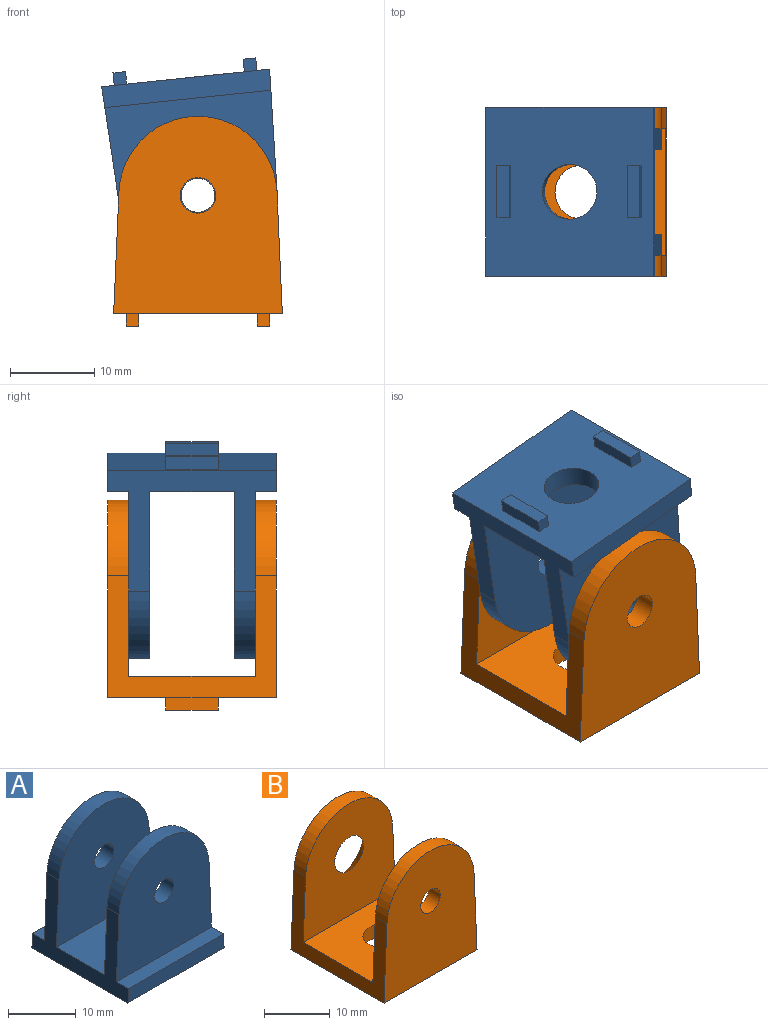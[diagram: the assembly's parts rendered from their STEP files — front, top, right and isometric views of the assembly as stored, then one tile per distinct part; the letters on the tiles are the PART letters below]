
ASSEMBLY  parts=2 mates=1
PART A: 27 faces, bbox 20x20x24.9 mm
  f0: plane 20.02x20mm, normal (0,0,-1), area 348.6mm2, adj f2,f4,f9,f10,f11,f12,f14,f15
  f1: plane 20.89x19.8mm, normal (0,1,0), area 347.9mm2, adj f2,f3,f4,f5,f8
  f2: plane 20x14.41mm, normal (1,0,0.04), area 109.7mm2, adj f0,f1,f3,f6,f7,f8,f9,f19
  f3: cylinder r=9.39mm len=18.76mm, axis (0,1,0), area 71.7mm2, adj f1,f2,f4,f6
  f4: plane 20x14.41mm, normal (-1,0,0.04), area 109.7mm2, adj f0,f1,f3,f6,f7,f8,f9,f19
  f5: cylinder r=2mm len=4mm, axis (0,1,0), area 31.4mm2, adj f1,f6
  f6: plane 20.89x19.8mm, normal (0,-1,0), area 347.9mm2, adj f2,f3,f4,f5,f7
  f7: plane 19.8x10mm, normal (0,0,1), area 164.8mm2, adj f2,f4,f6,f18,f22
  f8: plane 19.8x2.5mm, normal (0,0,1), area 49.5mm2, adj f1,f2,f4,f9
  f9: plane 20.02x2.5mm, normal (0,1,0), area 49.8mm2, adj f0,f2,f4,f8
  f10: plane 6.2x1.5mm, normal (-1,0,0), area 9.3mm2, adj f0,f11,f13,f25
  f11: plane 1.5x1.5mm, normal (0,1,0), area 2.2mm2, adj f0,f10,f12,f13
  f12: plane 6.2x1.5mm, normal (1,0,0), area 9.3mm2, adj f0,f11,f13,f25
  f13: plane 6.2x1.5mm, normal (0,0,-1), area 9.3mm2, adj f10,f11,f12,f25
  f14: plane 6.2x1.5mm, normal (-1,0,0), area 9.3mm2, adj f0,f15,f17,f26
  f15: plane 1.5x1.5mm, normal (0,1,0), area 2.2mm2, adj f0,f14,f16,f17
  f16: plane 6.2x1.5mm, normal (1,0,0), area 9.3mm2, adj f0,f15,f17,f26
  f17: plane 6.2x1.5mm, normal (0,0,-1), area 9.3mm2, adj f14,f15,f16,f26
  f18: cylinder r=3.25mm len=6.5mm, axis (0,0,-1), area 51.1mm2, adj f0,f7
  f19: plane 20.89x19.8mm, normal (0,-1,0), area 347.9mm2, adj f2,f4,f20,f21,f23
  f20: cylinder r=9.39mm len=18.76mm, axis (0,-1,0), area 71.7mm2, adj f2,f4,f19,f22
  f21: cylinder r=2mm len=4mm, axis (0,-1,0), area 31.4mm2, adj f19,f22
  f22: plane 20.89x19.8mm, normal (0,1,0), area 347.9mm2, adj f2,f4,f7,f20,f21
  f23: plane 19.8x2.5mm, normal (0,0,1), area 49.5mm2, adj f2,f4,f19,f24
  f24: plane 20.02x2.5mm, normal (0,-1,0), area 49.8mm2, adj f0,f2,f4,f23
  f25: plane 1.5x1.5mm, normal (0,-1,0), area 2.2mm2, adj f0,f10,f12,f13
  f26: plane 1.5x1.5mm, normal (0,-1,0), area 2.2mm2, adj f0,f14,f16,f17
PART B: 23 faces, bbox 20x20x24.9 mm
  f0: plane 20x20mm, normal (0,0,-1), area 349.2mm2, adj f1,f3,f4,f7,f8,f9,f11,f12
  f1: plane 20x14.41mm, normal (1,0,0.04), area 109.7mm2, adj f0,f2,f4,f5,f6,f15,f16,f17
  f2: plane 19.78x15mm, normal (0,0,1), area 264.6mm2, adj f1,f3,f6,f17,f22
  f3: plane 20x14.41mm, normal (-1,0,0.04), area 109.7mm2, adj f0,f2,f4,f5,f6,f15,f16,f17
  f4: plane 23.38x20mm, normal (0,1,0), area 311.1mm2, adj f0,f1,f3,f5,f21
  f5: cylinder r=9.38mm len=18.74mm, axis (0,1,0), area 71.6mm2, adj f1,f3,f4,f6
  f6: plane 20.88x19.78mm, normal (0,-1,0), area 329.7mm2, adj f1,f2,f3,f5,f21
  f7: plane 6.2x1.5mm, normal (-1,0,0), area 9.3mm2, adj f0,f8,f10,f18
  f8: plane 1.5x1.5mm, normal (0,1,0), area 2.3mm2, adj f0,f7,f9,f10
  f9: plane 6.2x1.5mm, normal (1,0,0), area 9.3mm2, adj f0,f8,f10,f18
  f10: plane 6.2x1.5mm, normal (0,0,-1), area 9.3mm2, adj f7,f8,f9,f18
  f11: plane 6.2x1.5mm, normal (-1,0,0), area 9.3mm2, adj f0,f12,f14,f19
  f12: plane 1.5x1.5mm, normal (0,1,0), area 2.3mm2, adj f0,f11,f13,f14
  f13: plane 6.2x1.5mm, normal (1,0,0), area 9.3mm2, adj f0,f12,f14,f19
  f14: plane 6.2x1.5mm, normal (0,0,-1), area 9.3mm2, adj f11,f12,f13,f19
  f15: plane 23.38x20mm, normal (0,-1,0), area 395.8mm2, adj f0,f1,f3,f16,f20
  f16: cylinder r=9.38mm len=18.74mm, axis (0,-1,0), area 71.6mm2, adj f1,f3,f15,f17
  f17: plane 20.88x19.78mm, normal (0,1,0), area 346.1mm2, adj f1,f2,f3,f16,f20
  f18: plane 1.5x1.5mm, normal (0,-1,0), area 2.3mm2, adj f0,f7,f9,f10
  f19: plane 1.5x1.5mm, normal (0,-1,0), area 2.3mm2, adj f0,f11,f13,f14
  f20: cylinder r=2.1mm len=4.2mm, axis (0,1,0), area 33mm2, adj f15,f17
  f21: cone r=2.1mm half-angle=45deg, axis (0,1,0), area 96.6mm2, adj f4,f6
  f22: cylinder r=3.2mm len=6.4mm, axis (0,0,-1), area 50.3mm2, adj f0,f2
PLACE A rot(axis=(0,1,0),174deg) t=(-14.57,4.62,24.01)mm
PLACE B t=(-13.1,7.12,-3.92)mm fixed
MATE revolute A.f5 <-> B.f20  axis (0,-1,0) through (-13.1,-10.38,10.08)mm
